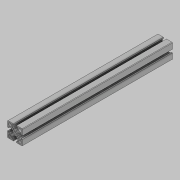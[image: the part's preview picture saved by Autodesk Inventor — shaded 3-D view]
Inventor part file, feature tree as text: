
AUTODESK INVENTOR PART (.ipt)
format: ipt  version: 2021.2 (Build 252289000, 289)  size: 202,240 bytes
history: native  units: in
note: dims shown in document units (in); Inventor stores cm internally (conversion verified against a paired STEP export)
features: other x2, extrude x1, sketch x1, projected_geometry x1
ambient origin geometry x8: Origin, YZ Plane, XZ Plane, XY Plane, X Axis, Y Axis, Z Axis, Center Point
bodies: Body1 (feature_tree)
feature tree (5):
  other  "ソリッド2"
  extrude  "押し出し1"  Depth=11.811in
  sketch  "スケッチ2"
  projected_geometry  "投影ループ1"
  other  "ソリッド1"
